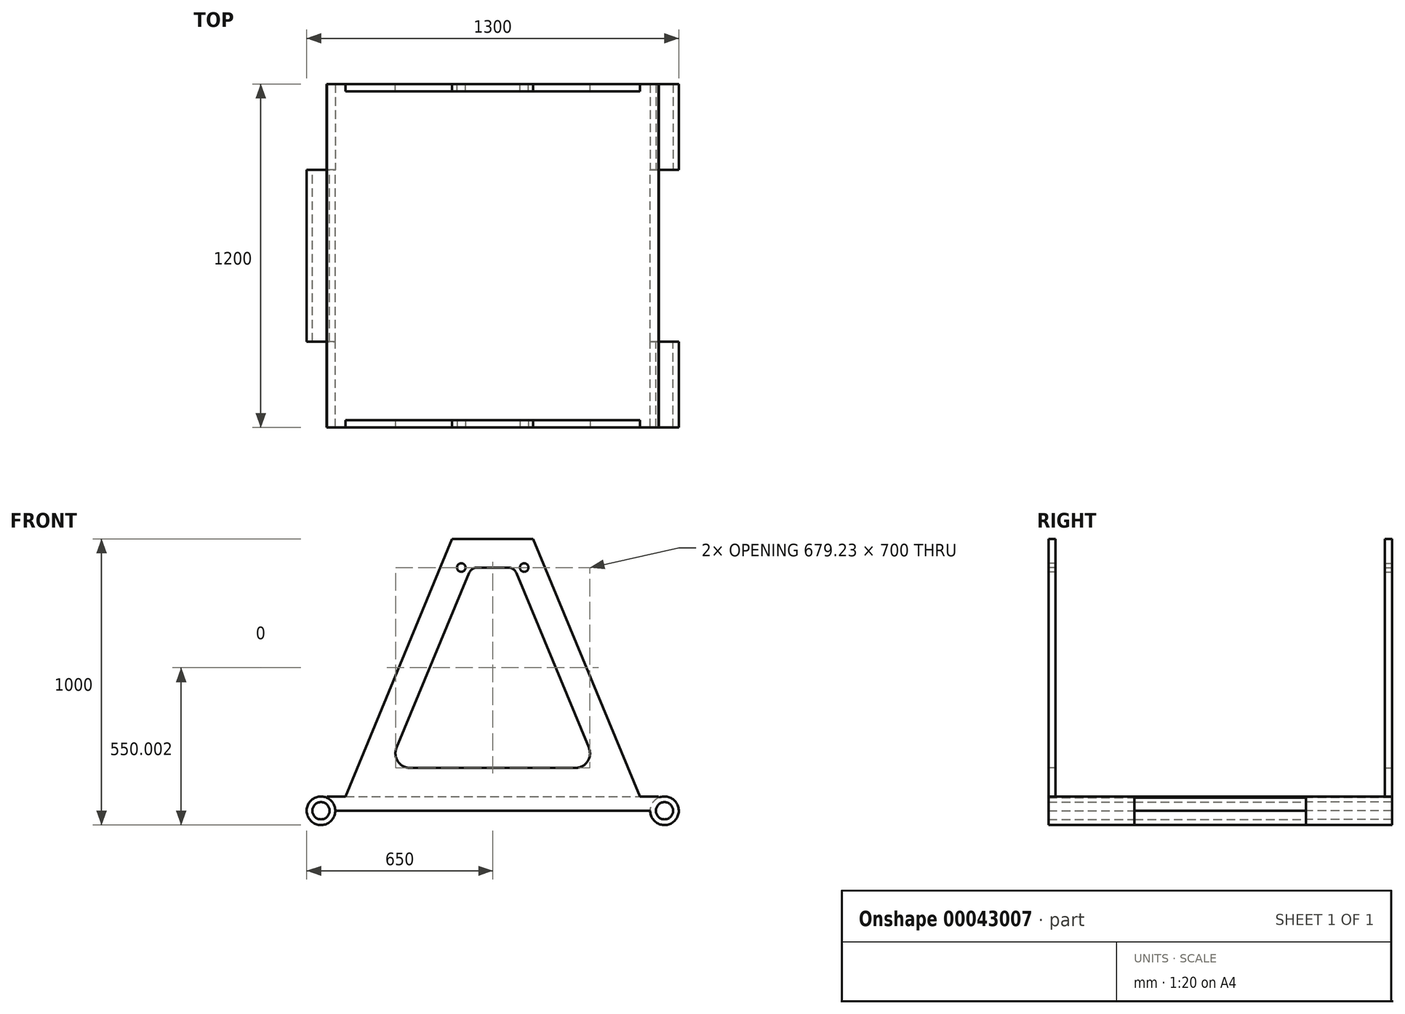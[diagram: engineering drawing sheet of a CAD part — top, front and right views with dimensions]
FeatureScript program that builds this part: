
annotation { "Feature Type Name" : "Feature", "Feature Type Description" : "" }
export const myFeature = defineFeature(function(context is Context, id is Id, definition is map)
    precondition{}
    {
        {
            var Q0;
            Q0=qCreatedBy(makeId("Front.planeOp"),FACE);
            var sketch = newSketch(context, id + "F0", { "sketchPlane" : qUnion([Q0])});
            skCircle(sketch, "E0.cCircle", {"center": v(0, 0) * mm, "radius": 1448.53 * mm, "construction": true});
            skLineSegment(sketch, "E0.0", {"start": v(600, -1448.53) * mm, "end": v(-600, -1448.53) * mm});
            skLineSegment(sketch, "E0.1", {"start": v(-600, -1448.53) * mm, "end": v(-1448.53, -600) * mm});
            skLineSegment(sketch, "E0.2", {"start": v(-1448.53, -600) * mm, "end": v(-1448.53, 600) * mm});
            skLineSegment(sketch, "E0.3", {"start": v(-1448.53, 600) * mm, "end": v(-600, 1448.53) * mm});
            skLineSegment(sketch, "E0.4", {"start": v(-600, 1448.53) * mm, "end": v(600, 1448.53) * mm});
            skLineSegment(sketch, "E0.5", {"start": v(600, 1448.53) * mm, "end": v(1448.53, 600) * mm});
            skLineSegment(sketch, "E0.6", {"start": v(1448.53, 600) * mm, "end": v(1448.53, -600) * mm});
            skLineSegment(sketch, "E0.7", {"start": v(1448.53, -600) * mm, "end": v(600, -1448.53) * mm});
            skPoint(sketch, "E0.0.midPoint", {"position": v(0, -1448.53) * mm});
            skLineSegment(sketch, "E1", {"start": v(0, 0) * mm, "end": v(-600, -1448.53) * mm});
            skLineSegment(sketch, "E2", {"start": v(0, 0) * mm, "end": v(600, -1448.53) * mm});
            skSolve(sketch);
        }
        {
            var Q0;
            Q0=qCreatedBy(makeId("Front.planeOp"),FACE);
            var sketch = newSketch(context, id + "F1", { "sketchPlane" : qUnion([Q0])});
            skLineSegment(sketch, "E3", {"start": v(-600, -1448.53) * mm, "end": v(-579.29, -1398.53) * mm});
            skLineSegment(sketch, "E4", {"start": v(-579.29, -1398.53) * mm, "end": v(579.29, -1398.53) * mm});
            skLineSegment(sketch, "E5", {"start": v(579.29, -1398.53) * mm, "end": v(600, -1448.53) * mm});
            skLineSegment(sketch, "E6", {"start": v(600, -1448.53) * mm, "end": v(-600, -1448.53) * mm});
            skSolve(sketch);
        }
        {
            var Q0;
            Q0 = qSketchRegion(id + "F1", true);
            extrude(context, id + "F2", {"entities" : qUnion([Q0]), "depth" : 600 * mm});
        }
        {
            var Q0;
            Q0=makeQuery(id+"F0.imprint","IMPRINT",FACE,{"disambiguationData":[TD([[makeQuery(id+"F0.imprint","IMPRINT",EDGE,{"derivedFrom":sQuery(id+"F0.wireOp",EDGE,"E0.1")}),-1.0]])]});
            var sketch = newSketch(context, id + "F3", { "sketchPlane" : qUnion([Q0])});
            skCircle(sketch, "E7", {"center": v(-600, -1448.53) * mm, "radius": 50 * mm});
            skCircle(sketch, "E8", {"center": v(600, -1448.53) * mm, "radius": 50 * mm});
            skSolve(sketch);
        }
        {
            var Q0;
            Q0 = qSketchRegion(id + "F3", true);
            var Q1;
            Q1=makeQuery(id+"F2.opExtrude","CAP_FACE",FACE,{"disambiguationData":[OSD([sQuery(id+"F1.wireOp",EDGE,"E3"),sQuery(id+"F1.wireOp",EDGE,"E4"),sQuery(id+"F1.wireOp",EDGE,"E5"),sQuery(id+"F1.wireOp",EDGE,"E6")])],"isStart":false});
            var Q2;
            Q2=makeQuery(id+"F2.opExtrude","CAP_FACE",FACE,{"disambiguationData":[OSD([sQuery(id+"F1.wireOp",EDGE,"E3"),sQuery(id+"F1.wireOp",EDGE,"E4"),sQuery(id+"F1.wireOp",EDGE,"E5"),sQuery(id+"F1.wireOp",EDGE,"E6")])],"isStart":true});
            extrude(context, id + "F4", {"entities" : qUnion([Q0]), "operationType" : NewBodyOperationType.ADD, "endBound" : BoundingType.UP_TO_SURFACE, "endBoundEntityFace" : qUnion([Q1]), "depth" : 25 * mm});
        }
        {
            var Q0;
            Q0=qCreatedBy(makeId("Front.planeOp"),FACE);
            var sketch = newSketch(context, id + "F5", { "sketchPlane" : qUnion([Q0])});
            skCircle(sketch, "E9.1", {"center": v(600, -1448.53) * mm, "radius": 50 * mm});
            skSolve(sketch);
        }
        {
            var Q0;
            Q0 = qSketchRegion(id + "F5", true);
            extrude(context, id + "F6", {"entities" : qUnion([Q0]), "operationType" : NewBodyOperationType.REMOVE, "endBound" : BoundingType.SYMMETRIC, "depth" : 600 * mm});
        }
        {
            var Q0;
            Q0=makeQuery(id+"F4.boolean.opBoolean","MERGE",FACE,{"derivedFrom":[makeQuery(id+"F2.opExtrude","CAP_FACE",FACE,{"disambiguationData":[OSD([sQuery(id+"F1.wireOp",EDGE,"E3"),sQuery(id+"F1.wireOp",EDGE,"E4"),sQuery(id+"F1.wireOp",EDGE,"E5"),sQuery(id+"F1.wireOp",EDGE,"E6")])],"isStart":false}),makeQuery(id+"F4.opExtrude","CAP_FACE",FACE,{"disambiguationData":[OSD([sQuery(id+"F3.wireOp",EDGE,"E7")])],"isStart":false}),makeQuery(id+"F4.opExtrude","CAP_FACE",FACE,{"disambiguationData":[OSD([sQuery(id+"F3.wireOp",EDGE,"E8")])],"isStart":false})]});
            var sketch = newSketch(context, id + "F7", { "sketchPlane" : qUnion([Q0])});
            skCircle(sketch, "E10.0", {"center": v(-600, -1448.53) * mm, "radius": 50 * mm});
            skSolve(sketch);
        }
        {
            var Q0;
            Q0 = qSketchRegion(id + "F7", true);
            var Q1;
            Q1=makeQuery(id+"F6.boolean.opBoolean","COPY",FACE,{"derivedFrom":makeQuery(id+"F6.opExtrude","CAP_FACE",FACE,{"disambiguationData":[OSD([sQuery(id+"F5.wireOp",EDGE,"E9.1")])],"isStart":false})});
            extrude(context, id + "F8", {"entities" : qUnion([Q0]), "operationType" : NewBodyOperationType.REMOVE, "endBound" : BoundingType.UP_TO_SURFACE, "oppositeDirection" : true, "endBoundEntityFace" : qUnion([Q1]), "depth" : 25 * mm});
        }
        {
            var Q0;
            Q0=qCreatedBy(makeId("Front.planeOp"),FACE);
            var sketch = newSketch(context, id + "F9", { "sketchPlane" : qUnion([Q0])});
            skCircle(sketch, "E11.0", {"center": v(-600, -1448.53) * mm, "radius": 30 * mm});
            skLineSegment(sketch, "E12", {"start": v(0, -1457.24) * mm, "end": v(0, -709.99) * mm, "construction": true});
            skCircle(sketch, "E13.MirrorC", {"center": v(600, -1448.53) * mm, "radius": 30 * mm});
            skSolve(sketch);
        }
        {
            var Q0;
            Q0 = qSketchRegion(id + "F9", true);
            extrude(context, id + "F10", {"entities" : qUnion([Q0]), "operationType" : NewBodyOperationType.REMOVE, "endBound" : BoundingType.THROUGH_ALL, "depth" : 25 * mm});
        }
        {
            var Q0;
            Q0=makeQuery(id+"F4.boolean.opBoolean","MERGE",FACE,{"derivedFrom":[makeQuery(id+"F2.opExtrude","CAP_FACE",FACE,{"disambiguationData":[OSD([sQuery(id+"F1.wireOp",EDGE,"E3"),sQuery(id+"F1.wireOp",EDGE,"E4"),sQuery(id+"F1.wireOp",EDGE,"E5"),sQuery(id+"F1.wireOp",EDGE,"E6")])],"isStart":false}),makeQuery(id+"F4.opExtrude","CAP_FACE",FACE,{"disambiguationData":[OSD([sQuery(id+"F3.wireOp",EDGE,"E7")])],"isStart":false}),makeQuery(id+"F4.opExtrude","CAP_FACE",FACE,{"disambiguationData":[OSD([sQuery(id+"F3.wireOp",EDGE,"E8")])],"isStart":false})]});
            var sketch = newSketch(context, id + "F11", { "sketchPlane" : qUnion([Q0])});
            skLineSegment(sketch, "E14.0", {"start": v(-141.55, -498.53) * mm, "end": v(-514.35, -1398.53) * mm});
            skLineSegment(sketch, "E14.1", {"start": v(141.55, -498.53) * mm, "end": v(514.35, -1398.53) * mm});
            skLineSegment(sketch, "E15", {"start": v(-141.55, -498.53) * mm, "end": v(141.55, -498.53) * mm});
            skLineSegment(sketch, "E16", {"start": v(-514.35, -1398.53) * mm, "end": v(514.35, -1398.53) * mm});
            skLineSegment(sketch, "E17.0", {"start": v(-82.4, -617.05) * mm, "end": v(-336.05, -1229.4) * mm});
            skLineSegment(sketch, "E17.1", {"start": v(-54.7, -598.53) * mm, "end": v(54.7, -598.53) * mm});
            skLineSegment(sketch, "E17.2", {"start": v(82.4, -617.05) * mm, "end": v(336.05, -1229.4) * mm});
            skLineSegment(sketch, "E17.3", {"start": v(-289.85, -1298.53) * mm, "end": v(289.85, -1298.53) * mm});
            skPoint(sketch, "E18.visualSharp", {"position": v(364.69, -1298.53) * mm});
            skArc(sketch, "E18.filletArc", {"start": v(289.85, -1298.53) * mm, "mid": v(331.43, -1276.3) * mm, "end": v(336.05, -1229.4) * mm});
            skPoint(sketch, "E19.visualSharp", {"position": v(-364.69, -1298.53) * mm});
            skArc(sketch, "E19.filletArc", {"start": v(-336.05, -1229.4) * mm, "mid": v(-331.43, -1276.3) * mm, "end": v(-289.85, -1298.53) * mm});
            skPoint(sketch, "E20.visualSharp", {"position": v(74.74, -598.53) * mm});
            skArc(sketch, "E20.filletArc", {"start": v(82.4, -617.05) * mm, "mid": v(71.36, -603.58) * mm, "end": v(54.7, -598.53) * mm});
            skPoint(sketch, "E21.visualSharp", {"position": v(-74.74, -598.53) * mm});
            skArc(sketch, "E21.filletArc", {"start": v(-54.7, -598.53) * mm, "mid": v(-71.36, -603.58) * mm, "end": v(-82.4, -617.05) * mm});
            skCircle(sketch, "E22", {"center": v(-110, -598.53) * mm, "radius": 15 * mm});
            skLineSegment(sketch, "E23", {"start": v(0, -498.53) * mm, "end": v(0, -598.53) * mm, "construction": true});
            skCircle(sketch, "E24.MirrorC", {"center": v(110, -598.53) * mm, "radius": 15 * mm});
            skSolve(sketch);
        }
        {
            var Q0;
            Q0 = qSketchRegion(id + "F11", true);
            extrude(context, id + "F12", {"entities" : qUnion([Q0]), "operationType" : NewBodyOperationType.ADD, "oppositeDirection" : true, "depth" : 25 * mm});
        }
        {
            var Q0;
            Q0=makeQuery(id+"F2.opExtrude","SWEPT_BODY",BODY,{"disambiguationData":[OSD([sQuery(id+"F1.wireOp",EDGE,"E3"),sQuery(id+"F1.wireOp",EDGE,"E4"),sQuery(id+"F1.wireOp",EDGE,"E5"),sQuery(id+"F1.wireOp",EDGE,"E6")])]});
            var Q1;
            Q1=qCreatedBy(makeId("Front.planeOp"),FACE);
            mirror(context, id + "F13", {"operationType" : NewBodyOperationType.ADD, "entities" : qUnion([Q0]), "mirrorPlane" : qUnion([Q1])});
        }
    });
